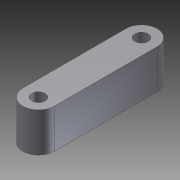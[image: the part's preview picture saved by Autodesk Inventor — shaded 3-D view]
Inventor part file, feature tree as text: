
AUTODESK INVENTOR PART (.ipt)
format: ipt  version: 2011 SP2 (Build 150309200, 309)  size: 90,624 bytes
history: native  units: mm
features: sketch x2, extrude x1, hole x1
ambient origin geometry x8: Origin, YZ Plane, XZ Plane, XY Plane, X Axis, Y Axis, Z Axis, Center Point
bodies: Solid1 (feature_tree)
feature tree (4):
  extrude  "Extrusion1"  Depth=26.335787mm
  hole  "Hole1"  [1 undecoded]
  sketch  "Sketch1"  dims[d0=4.0mm d6=26.335787mm]
  sketch  "Sketch2"  dims[d14=10.0mm d15=0.0mm d16=3.4mm d17=6.0mm d18=4.4mm d19=3.0mm d20=90.0deg d21=8.0mm d22=20.594885mm]
note: 1 required parameter value undecoded (feature->parameter linkage not recoverable at this tier; creation-order binding heuristic only, values carry confidence <= 0.55)
